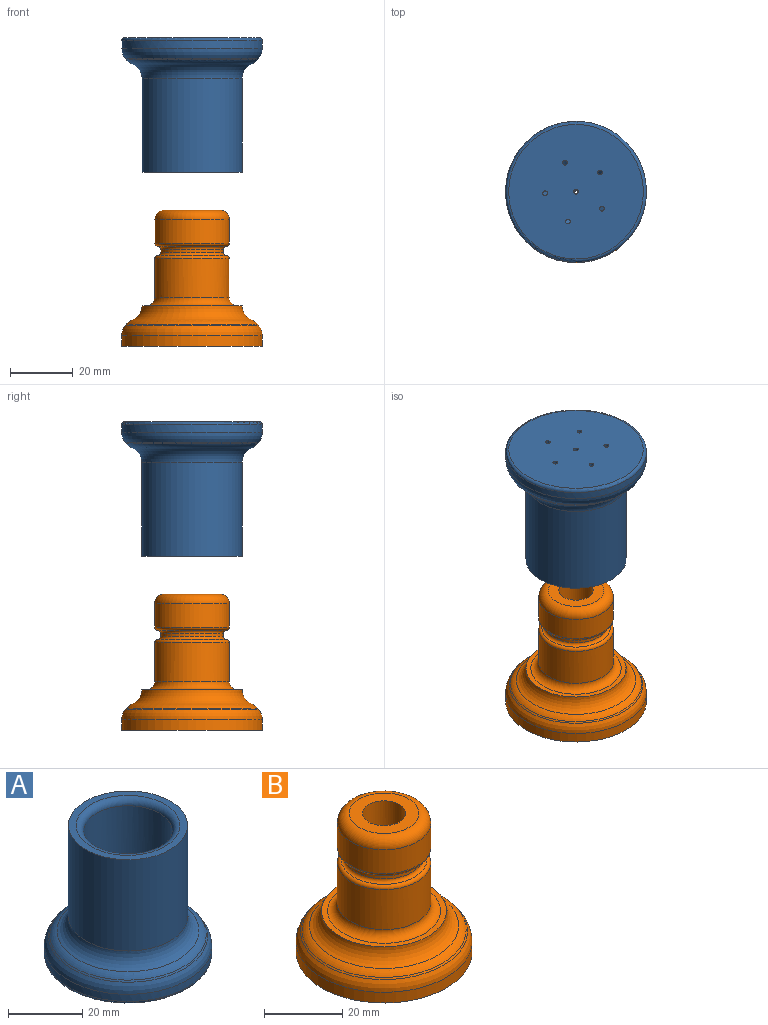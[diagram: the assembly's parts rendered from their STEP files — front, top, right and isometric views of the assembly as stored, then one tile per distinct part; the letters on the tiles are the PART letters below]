
ASSEMBLY  parts=2 mates=1
PART A: 26 faces, bbox 48.7x48.7x43 mm
  f0: cylinder r=6.9mm len=13.8mm, axis (0,0,-1), area 173.8mm2, adj f1,f10
  f1: plane 19.9x19.9mm, normal (0,0,1), area 161.5mm2, adj f0,f24
  f2: cylinder r=22.5mm len=45mm, axis (0,0,1), area 331.1mm2, adj f7,f20
  f3: plane 43x43mm, normal (0,0,-1), area 1441.6mm2, adj f13,f14,f15,f16,f17,f18,f20
  f4: torus R=21mm, axis (0,0,-1), area 630.1mm2, adj f6,f22
  f5: cone r=22.5mm half-angle=39.6deg, axis (0,0,-1), area 74.6mm2, adj f6,f7
  f6: torus R=17.14mm, axis (0,0,-1), area 305.3mm2, adj f4,f5
  f7: torus R=17.5mm, axis (0,0,1), area 480.1mm2, adj f2,f5
  f8: cylinder r=15mm len=30mm, axis (0,0,-1), area 94.2mm2, adj f12,f19
  f9: plane 26x26mm, normal (0,0,-1), area 22mm2, adj f11,f12
  f10: cone r=11.9mm half-angle=45deg, axis (0,0,-1), area 357.2mm2, adj f0,f11
  f11: torus R=12.73mm, axis (0,0,-1), area 118.3mm2, adj f9,f10
  f12: torus R=13mm, axis (0,0,-1), area 281.7mm2, adj f8,f9
  f13: cylinder r=0.75mm len=1.5mm, axis (0,0,-1), area 4.7mm2, adj f3,f19
  f14: cylinder r=0.75mm len=1.5mm, axis (0,0,-1), area 4.7mm2, adj f3,f19
  f15: cylinder r=0.75mm len=1.5mm, axis (0,0,-1), area 4.7mm2, adj f3,f19
  f16: cylinder r=0.75mm len=1.5mm, axis (0,0,-1), area 4.7mm2, adj f3,f19
  f17: cylinder r=0.75mm len=1.5mm, axis (0,0,-1), area 4.7mm2, adj f3,f19
  f18: cylinder r=0.75mm len=1.5mm, axis (0,0,-1), area 4.7mm2, adj f3,f19
  f19: plane 30x30mm, normal (0,0,1), area 696.3mm2, adj f8,f13,f14,f15,f16,f17,f18
  f20: torus R=21.5mm, axis (0,0,-1), area 218.5mm2, adj f2,f3
  f21: cylinder r=11.95mm len=25.99mm, axis (0,0,-1), area 1951.4mm2, adj f24,f25
  f22: cylinder r=16mm len=32mm, axis (0,0,-1), area 3015.9mm2, adj f4,f23
  f23: plane 32x32mm, normal (0,0,1), area 192.9mm2, adj f22,f25
  f24: torus R=9.95mm, axis (0,0,1), area 221.5mm2, adj f1,f21
  f25: torus R=13.95mm, axis (0,0,-1), area 250.2mm2, adj f21,f23
PART B: 31 faces, bbox 48.7x48.7x43.5 mm
  f0: cylinder r=15mm len=30mm, axis (0,0,-1), area 94.2mm2, adj f15,f23
  f1: cylinder r=5.5mm len=34.5mm, axis (0,0,-1), area 1192.2mm2, adj f13,f28
  f2: cylinder r=11.93mm len=23.87mm, axis (0,0,-1), area 937.4mm2, adj f25,f30
  f3: cylinder r=10mm len=20mm, axis (0,0,-1), area 63mm2, adj f26,f27
  f4: cylinder r=11.93mm len=23.87mm, axis (0,0,-1), area 562.4mm2, adj f24,f29
  f5: plane 32x32mm, normal (0,0,1), area 149.6mm2, adj f8,f30
  f6: cylinder r=22.5mm len=45mm, axis (0,0,1), area 472.5mm2, adj f7,f11
  f7: plane 45x45mm, normal (0,0,-1), area 1584.9mm2, adj f6,f16,f17,f18,f19,f20,f21,f22
  f8: torus R=21mm, axis (0,0,-1), area 630.1mm2, adj f5,f10
  f9: cone r=22.5mm half-angle=39.6deg, axis (0,0,-1), area 74.6mm2, adj f10,f11
  f10: torus R=17.14mm, axis (0,0,-1), area 305.3mm2, adj f8,f9
  f11: torus R=17.5mm, axis (0,0,1), area 480.1mm2, adj f6,f9
  f12: plane 26x26mm, normal (0,0,-1), area 127.8mm2, adj f14,f15
  f13: cone r=10.5mm half-angle=45deg, axis (0,0,-1), area 302.3mm2, adj f1,f14
  f14: torus R=11.33mm, axis (0,0,-1), area 104.4mm2, adj f12,f13
  f15: torus R=13mm, axis (0,0,-1), area 281.7mm2, adj f0,f12
  f16: cylinder r=0.5mm len=1mm, axis (0,0,-1), area 3.1mm2, adj f7,f23
  f17: cylinder r=0.5mm len=1mm, axis (0,0,-1), area 3.1mm2, adj f7,f23
  f18: cylinder r=0.5mm len=1mm, axis (0,0,-1), area 3.1mm2, adj f7,f23
  f19: cylinder r=0.5mm len=1mm, axis (0,0,-1), area 3.1mm2, adj f7,f23
  f20: cylinder r=0.5mm len=1mm, axis (0,0,-1), area 3.1mm2, adj f7,f23
  f21: cylinder r=0.5mm len=1mm, axis (0,0,-1), area 3.1mm2, adj f7,f23
  f22: cylinder r=0.5mm len=1mm, axis (0,0,-1), area 3.1mm2, adj f7,f23
  f23: plane 30x30mm, normal (0,0,1), area 701.4mm2, adj f0,f16,f17,f18,f19,f20,f21,f22
  f24: torus R=10.94mm, axis (0,0,1), area 112mm2, adj f4,f27
  f25: torus R=10.94mm, axis (0,0,1), area 112mm2, adj f2,f26
  f26: torus R=11mm, axis (0,0,1), area 100mm2, adj f3,f25
  f27: torus R=11mm, axis (0,0,1), area 100mm2, adj f3,f24
  f28: plane 17.87x17.87mm, normal (0,0,1), area 155.8mm2, adj f1,f29
  f29: torus R=8.94mm, axis (0,0,1), area 321.1mm2, adj f4,f28
  f30: torus R=14.44mm, axis (0,0,-1), area 316.9mm2, adj f2,f5
PLACE A rot(axis=(1,0,0),180deg) t=(-88.21,35.57,84.97)mm
PLACE B t=(-88.21,35.57,12.36)mm
MATE slider B.f0 <-> A.f0  axis (0,0,1) through (-88.21,35.57,12.36)mm
